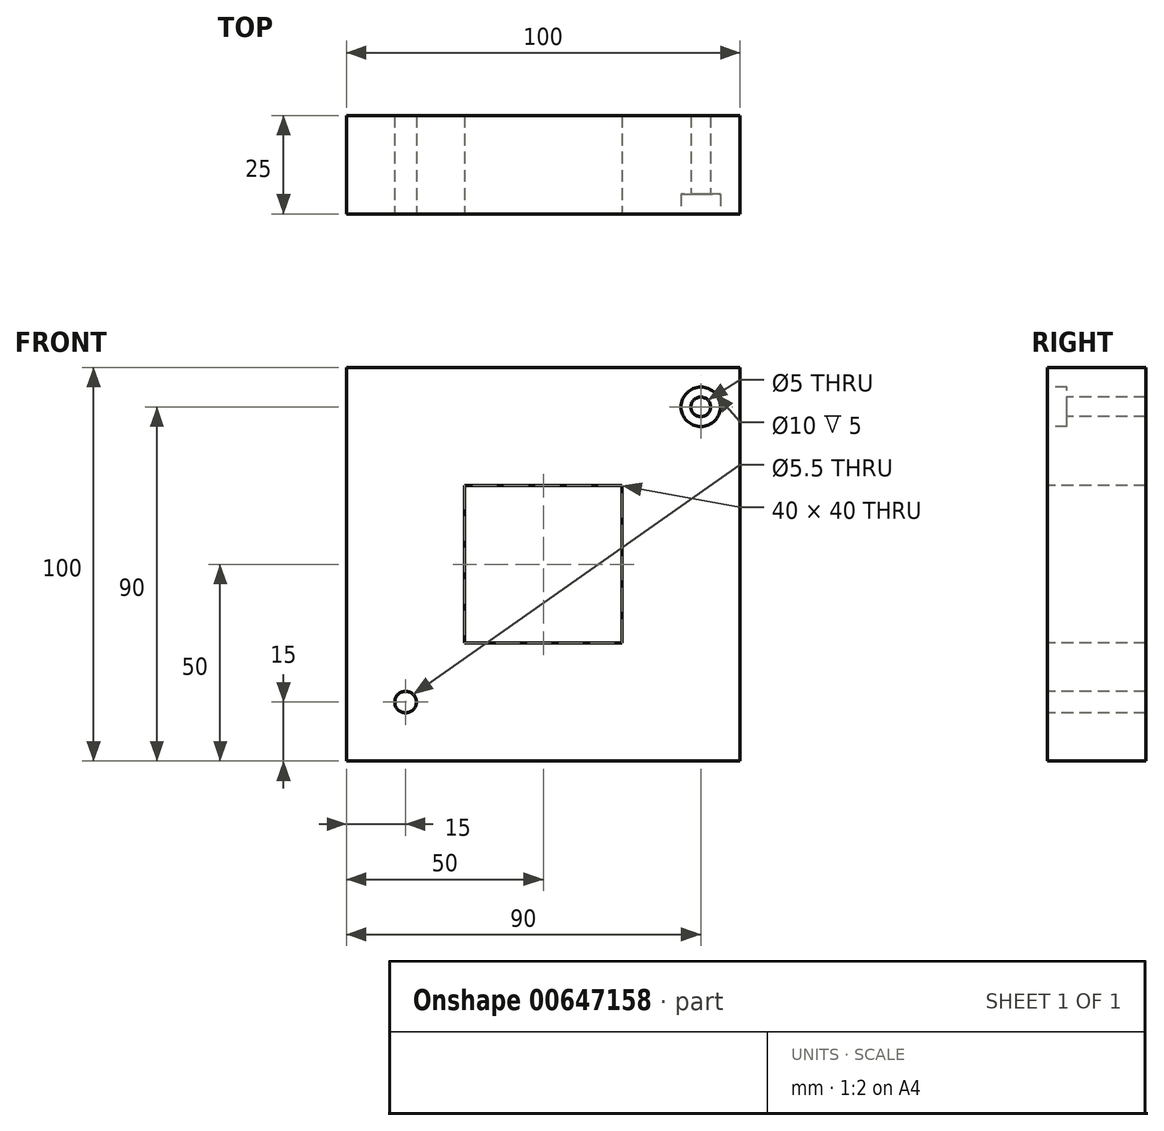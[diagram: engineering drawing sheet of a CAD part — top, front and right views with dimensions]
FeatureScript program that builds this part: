
annotation { "Feature Type Name" : "Feature", "Feature Type Description" : "" }
export const myFeature = defineFeature(function(context is Context, id is Id, definition is map)
    precondition{}
    {
        {
            var Q0;
            Q0=qCreatedBy(makeId("Front.planeOp"),FACE);
            var sketch = newSketch(context, id + "F0", { "sketchPlane" : qUnion([Q0])});
            skLineSegment(sketch, "E0.bottom", {"start": v(0, 0) * mm, "end": v(100, 0) * mm});
            skLineSegment(sketch, "E0.top", {"start": v(0, 100) * mm, "end": v(100, 100) * mm});
            skLineSegment(sketch, "E0.left", {"start": v(0, 0) * mm, "end": v(0, 100) * mm});
            skLineSegment(sketch, "E0.right", {"start": v(100, 0) * mm, "end": v(100, 100) * mm});
            skSolve(sketch);
        }
        {
            var Q0;
            Q0 = qSketchRegion(id + "F0", true);
            extrude(context, id + "F1", {"entities" : qUnion([Q0]), "depth" : 25 * mm, "offsetDistance" : 25 * mm});
        }
        {
            var Q0;
            Q0=makeQuery(id+"F1.opExtrude","CAP_FACE",FACE,{"disambiguationData":[OSD([sQuery(id+"F0.wireOp",EDGE,"E0.bottom"),sQuery(id+"F0.wireOp",EDGE,"E0.top"),sQuery(id+"F0.wireOp",EDGE,"E0.left"),sQuery(id+"F0.wireOp",EDGE,"E0.right")])],"isStart":false});
            var sketch = newSketch(context, id + "F2", { "sketchPlane" : qUnion([Q0])});
            skLineSegment(sketch, "E1.bottom", {"start": v(30, 70) * mm, "end": v(70, 70) * mm});
            skLineSegment(sketch, "E1.top", {"start": v(30, 30) * mm, "end": v(70, 30) * mm});
            skLineSegment(sketch, "E1.left", {"start": v(30, 70) * mm, "end": v(30, 30) * mm});
            skLineSegment(sketch, "E1.right", {"start": v(70, 70) * mm, "end": v(70, 30) * mm});
            skSolve(sketch);
        }
        {
            var Q0;
            Q0 = qSketchRegion(id + "F2", true);
            extrude(context, id + "F3", {"entities" : qUnion([Q0]), "operationType" : NewBodyOperationType.REMOVE, "oppositeDirection" : true, "depth" : 25 * mm, "offsetDistance" : 25 * mm});
        }
        {
            var Q0;
            Q0=makeQuery(id+"F1.opExtrude","CAP_FACE",FACE,{"disambiguationData":[OSD([sQuery(id+"F0.wireOp",EDGE,"E0.bottom"),sQuery(id+"F0.wireOp",EDGE,"E0.top"),sQuery(id+"F0.wireOp",EDGE,"E0.left"),sQuery(id+"F0.wireOp",EDGE,"E0.right")])],"isStart":false});
            var sketch = newSketch(context, id + "F4", { "sketchPlane" : qUnion([Q0])});
            skLineSegment(sketch, "E2.bottom", {"start": v(10, 90) * mm, "end": v(90, 90) * mm, "construction": true});
            skLineSegment(sketch, "E2.top", {"start": v(10, 10) * mm, "end": v(90, 10) * mm, "construction": true});
            skLineSegment(sketch, "E2.left", {"start": v(10, 90) * mm, "end": v(10, 10) * mm, "construction": true});
            skLineSegment(sketch, "E2.right", {"start": v(90, 90) * mm, "end": v(90, 10) * mm, "construction": true});
            skSolve(sketch);
        }
        {
            var Q0;
            Q0=sQuery(id+"F4.wireOp",VERTEX,"E2.right.start");
            var Q1;
            Q1=makeQuery(id+"F1.opExtrude","SWEPT_BODY",BODY,{"disambiguationData":[OSD([sQuery(id+"F0.wireOp",EDGE,"E0.bottom"),sQuery(id+"F0.wireOp",EDGE,"E0.top"),sQuery(id+"F0.wireOp",EDGE,"E0.left"),sQuery(id+"F0.wireOp",EDGE,"E0.right")])]});
            hole(context, id + "F5", {"style" : HoleStyle.C_BORE, "endStyle" : HoleEndStyle.THROUGH, "holeDiameter" : 5 * mm, "cBoreDiameter" : 10 * mm, "cBoreDepth" : 5 * mm, "majorDiameter" : 5 * mm, "isTappedThrough" : true, "tappedDepth" : 12 * mm, "tapClearance" : 3, "startFromSketch" : true, "locations" : qUnion([Q0]), "scope" : qUnion([Q1])});
        }
        {
            var Q0;
            Q0=makeQuery(id+"F1.opExtrude","CAP_FACE",FACE,{"disambiguationData":[OSD([sQuery(id+"F0.wireOp",EDGE,"E0.bottom"),sQuery(id+"F0.wireOp",EDGE,"E0.top"),sQuery(id+"F0.wireOp",EDGE,"E0.left"),sQuery(id+"F0.wireOp",EDGE,"E0.right")])],"isStart":false});
            var sketch = newSketch(context, id + "F6", { "sketchPlane" : qUnion([Q0])});
            skPoint(sketch, "E3", {"position": v(15, 15) * mm});
            skSolve(sketch);
        }
        {
            var Q0;
            Q0=sQuery(id+"F6.wireOp",VERTEX,"E3");
            var Q1;
            Q1=makeQuery(id+"F1.opExtrude","SWEPT_BODY",BODY,{"disambiguationData":[OSD([sQuery(id+"F0.wireOp",EDGE,"E0.bottom"),sQuery(id+"F0.wireOp",EDGE,"E0.top"),sQuery(id+"F0.wireOp",EDGE,"E0.left"),sQuery(id+"F0.wireOp",EDGE,"E0.right")])]});
            hole(context, id + "F7", {"style" : HoleStyle.SIMPLE, "endStyle" : HoleEndStyle.THROUGH, "standardTappedOrClearance" : lookupTablePath({ "standard" : "ISO", "fit" : "Normal", "size" : "M5", "type" : "Clearance" }), "standardBlindInLast" : lookupTablePath({ "fit" : "Standard", "standard" : "ISO", "size" : "M5", "type" : "Clearance" }), "holeDiameter" : 5.5 * mm, "majorDiameter" : 5 * mm, "isTappedThrough" : true, "tappedDepth" : 12 * mm, "tapClearance" : 3, "startFromSketch" : true, "locations" : qUnion([Q0]), "scope" : qUnion([Q1])});
        }
    });
